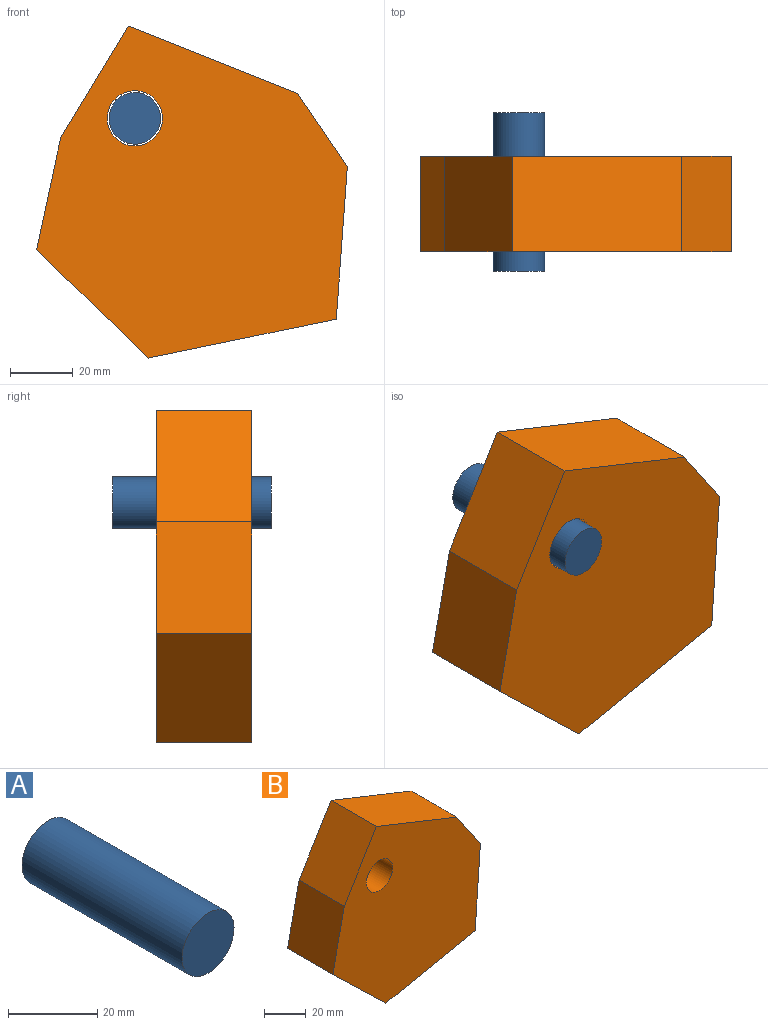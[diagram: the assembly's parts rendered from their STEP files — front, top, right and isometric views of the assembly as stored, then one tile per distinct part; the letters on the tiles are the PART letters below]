
ASSEMBLY  parts=2 mates=2
PART A: 3 faces, bbox 16.5x50.8x16.5 mm
  f0: cylinder r=8.26mm len=50.8mm, axis (0,1,0), area 2634.9mm2, adj f1,f2
  f1: plane 16.51x16.51mm, normal (0,-1,0), area 214.1mm2, adj f0
  f2: plane 16.51x16.51mm, normal (0,1,0), area 214.1mm2, adj f0
PART B: 10 faces, bbox 99.4x30.5x106.2 mm
  f0: plane 35.79x30.48mm, normal (-0.86,0,0.52), area 1274mm2, adj f1,f6,f7,f8
  f1: plane 35.79x30.48mm, normal (-0.98,0,0.21), area 1115.8mm2, adj f0,f2,f7,f8
  f2: plane 35.79x34.61mm, normal (-0.7,0,-0.72), area 1517.5mm2, adj f1,f3,f7,f8
  f3: plane 60.04x30.48mm, normal (0.2,0,-0.98), area 1868.9mm2, adj f2,f4,f7,f8
  f4: plane 48.8x30.48mm, normal (1,0,-0.07), area 1491.5mm2, adj f3,f5,f7,f8
  f5: plane 30.48x23.37mm, normal (0.83,0,0.56), area 862.7mm2, adj f4,f6,f7,f8
  f6: plane 54.13x30.48mm, normal (0.37,0,0.93), area 1776.3mm2, adj f0,f5,f7,f8
  f7: plane 106.19x99.38mm, normal (0,-1,0), area 7270.4mm2, adj f0,f1,f2,f3,f4,f5,f6,f9
  f8: plane 106.19x99.38mm, normal (0,1,0), area 7270.4mm2, adj f0,f1,f2,f3,f4,f5,f6,f9
  f9: cylinder r=8.83mm len=30.48mm, axis (0,-1,0), area 1690.4mm2, adj f7,f8
PLACE A rot(axis=(0,-1,0),90deg) t=(-29.65,20.05,-1.78)mm
PLACE B t=(-15.67,6.08,-37.62)mm fixed
MATE planar B.f7 <-> A.f0  axis (0,-1,0) through (-9.66,-24.4,-29.43)mm
MATE cylindrical B.f9 <-> A.f0  axis (0,-1,0) through (-29.65,-24.4,-1.78)mm
